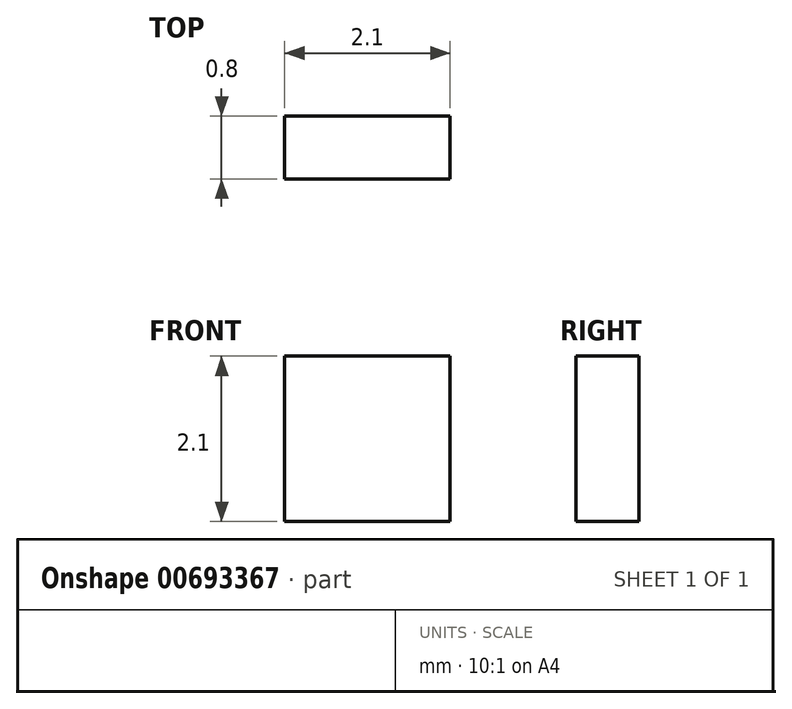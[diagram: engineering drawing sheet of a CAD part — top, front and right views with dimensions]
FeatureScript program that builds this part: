
annotation { "Feature Type Name" : "Feature", "Feature Type Description" : "" }
export const myFeature = defineFeature(function(context is Context, id is Id, definition is map)
    precondition{}
    {
        {
            var Q0;
            Q0=qCreatedBy(makeId("Front.planeOp"),FACE);
            var sketch = newSketch(context, id + "F0", { "sketchPlane" : qUnion([Q0])});
            skLineSegment(sketch, "E0.bottom", {"start": v(0, 0) * mm, "end": v(2.1, 0) * mm});
            skLineSegment(sketch, "E0.top", {"start": v(0, -2.1) * mm, "end": v(2.1, -2.1) * mm});
            skLineSegment(sketch, "E0.left", {"start": v(0, 0) * mm, "end": v(0, -2.1) * mm});
            skLineSegment(sketch, "E0.right", {"start": v(2.1, 0) * mm, "end": v(2.1, -2.1) * mm});
            skSolve(sketch);
        }
        {
            var Q0;
            Q0=makeQuery(id+"F0.imprint","IMPRINT",FACE,{"disambiguationData":[TD([[makeQuery(id+"F0.imprint","IMPRINT",EDGE,{"derivedFrom":sQuery(id+"F0.wireOp",EDGE,"E0.bottom")}),-1.0]])]});
            extrude(context, id + "F1", {"entities" : qUnion([Q0]), "depth" : 0.8 * mm, "offsetDistance" : 25 * mm});
        }
    });
